# Revit family: 1412xxx Cut
name_source: partatom
category: Lighting Fixtures
revit_build: Autodesk Revit 2018 (Build: 20170223_1515(x64)
units: mm (PartAtom-declared; Revit-internal decimal feet)

## family parameters
Always vertical = Yes
Cut with Voids When Loaded = No
Light Source = No
OmniClass Number = 23.80.70.00
OmniClass Title = Lighting
Part Type = Normal
Room Calculation Point = No
Round Connector Dimension = Use Diameter
Shared = No
Work Plane-Based = No

## types (1)
- CE
    Apparent Load = 0 VA
    Dimmable = No
    Driver Required = No
    Efficacy (lm/W) = Lamp Dependent
    Electrical Class = CE (Class II)
    Lamp = LED GU10
    Length of Cable Supplied = 3000mm
    Light Source Fixed = No
    Location Rating = IP20
    Main Finish = Various
    Main Material = Metal - Aluminium
    Power (W) = Lamp Dependent
    Product Location = Indoor
    Product Name = Cut
    Product SKU = 1412001
    Wattage Comments = 6W MAX LED GU10

## geometry (parser evidence)
native form markers: Sweep x2
no freeform markers — native parametric forms only
